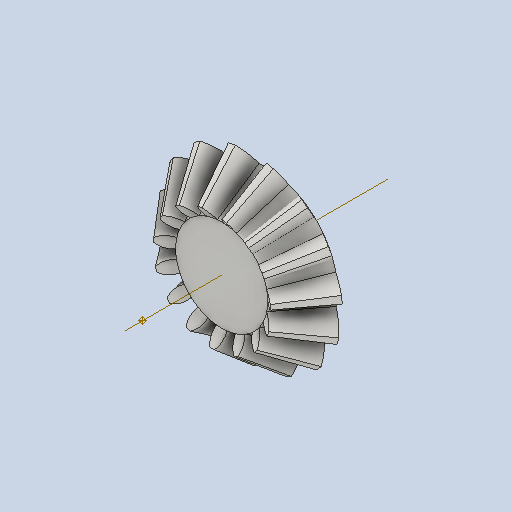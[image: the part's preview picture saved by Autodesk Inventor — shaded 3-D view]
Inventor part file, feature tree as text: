
AUTODESK INVENTOR PART (.ipt)
format: ipt  version: 2025.2 (Build 292293000, 293)  size: 487,424 bytes
history: native  units: mm
features: other x24, loft x2, pattern_circular x2
ambient origin geometry x6: Origin, XZ Plane, X Axis, Y Axis, Z Axis, Center Point
bodies: Solid1 (feature_tree)
feature tree (28):
  other  "Top Point"
  other  "Mesh Plane2"
  other  "Teeth Body"
  other  "Start Point"
  other  "Tooth Plane"
  other  "Start Sketch"
  other  "End Point"
  other  "3D Sketch Right"
  other  "End Plane Right"
  loft  "Loft Right"
  pattern_circular  "Circular Pattern Right"  [2 undecoded]
  other  "3D Sketch Left"
  other  "End Plane Left"
  loft  "Loft Left"
  pattern_circular  "Circular Pattern Left"  [2 undecoded]
  other  "Fix Body"
  other  "Mesh Plane"
  other  "Top Plane"
  other  "Teeth Body Sketch"
  other  "End Plane"
  other  "End Sketch"
  other  "Helical Curve Left"
  other  "End Sketch Left"
  other  "Body Sketch"
  other  "Srf1"
  other  "Helical Curve Right"
  other  "End Sketch Right"
  other  "Pitch Diameter"
note: 4 required parameter values undecoded (feature->parameter linkage not recoverable at this tier; creation-order binding heuristic only, values carry confidence <= 0.55)
